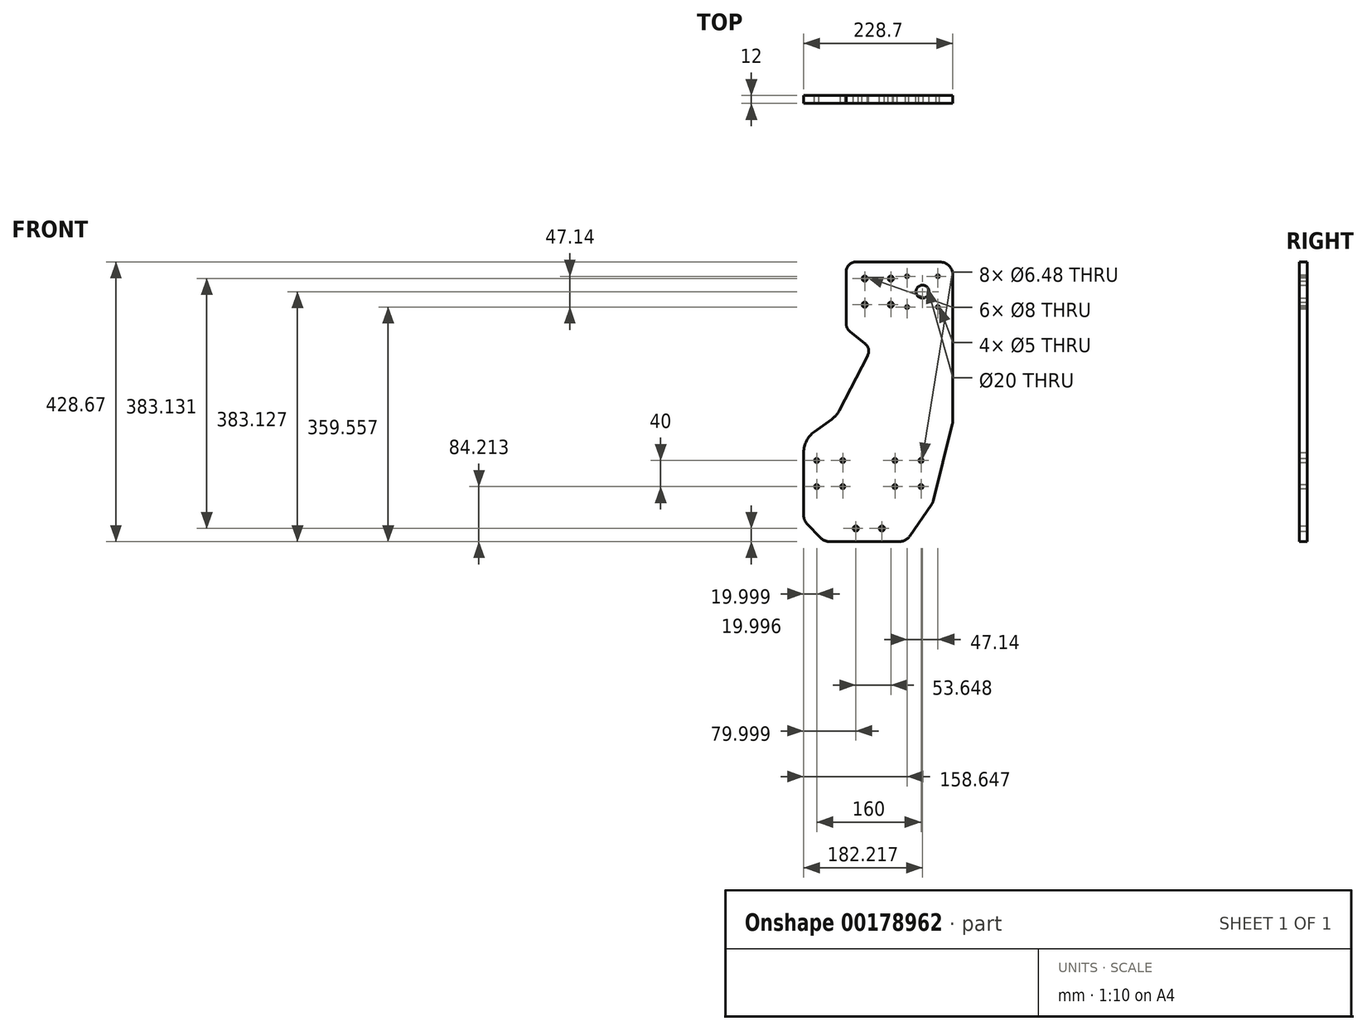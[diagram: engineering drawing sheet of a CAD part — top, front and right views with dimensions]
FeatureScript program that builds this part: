
annotation { "Feature Type Name" : "Feature", "Feature Type Description" : "" }
export const myFeature = defineFeature(function(context is Context, id is Id, definition is map)
    precondition{}
    {
        {
            var Q0;
            Q0=qCreatedBy(makeId("Front.planeOp"),FACE);
            var sketch = newSketch(context, id + "F0", { "sketchPlane" : qUnion([Q0])});
            skLineSegment(sketch, "E0.top", {"start": v(85.23, 205) * mm, "end": v(25.3, 205) * mm});
            skPoint(sketch, "E0.middle", {"position": v(0, 0) * mm});
            skLineSegment(sketch, "E1", {"start": v(135.36, -38.58) * mm, "end": v(135.36, 185) * mm});
            skLineSegment(sketch, "E2", {"start": v(115.36, 205) * mm, "end": v(85.23, 205) * mm});
            skLineSegment(sketch, "E3", {"start": v(-50.18, -36.07) * mm, "end": v(-76.73, -55.2) * mm});
            skCircle(sketch, "E4", {"center": v(-73.34, -139.46) * mm, "radius": 3.24 * mm});
            skCircle(sketch, "E5", {"center": v(-73.34, -99.46) * mm, "radius": 3.24 * mm});
            skCircle(sketch, "E6", {"center": v(-33.34, -99.46) * mm, "radius": 3.24 * mm});
            skCircle(sketch, "E7", {"center": v(-33.34, -139.46) * mm, "radius": 3.24 * mm});
            skCircle(sketch, "E8", {"center": v(46.66, -99.46) * mm, "radius": 3.24 * mm});
            skCircle(sketch, "E9", {"center": v(46.66, -139.46) * mm, "radius": 3.24 * mm});
            skCircle(sketch, "E10", {"center": v(86.66, -139.46) * mm, "radius": 3.24 * mm});
            skCircle(sketch, "E11", {"center": v(86.66, -99.46) * mm, "radius": 3.24 * mm});
            skCircle(sketch, "E12", {"center": v(-13.34, -203.67) * mm, "radius": 4 * mm});
            skCircle(sketch, "E13", {"center": v(26.66, -203.67) * mm, "radius": 4 * mm});
            skPoint(sketch, "E14.orphan", {"position": v(-84.77, 205) * mm});
            skPoint(sketch, "E15.visualSharp", {"position": v(-92.99, -66.91) * mm});
            skArc(sketch, "E15.filletArc", {"start": v(-76.73, -55.2) * mm, "mid": v(-88.79, -69.1) * mm, "end": v(-93.34, -86.95) * mm});
            skCircle(sketch, "E16", {"center": v(0.3, 179.46) * mm, "radius": 4 * mm});
            skCircle(sketch, "E17", {"center": v(40.3, 179.46) * mm, "radius": 4 * mm});
            skCircle(sketch, "E18", {"center": v(0.3, 139.46) * mm, "radius": 4 * mm});
            skCircle(sketch, "E19", {"center": v(40.3, 139.46) * mm, "radius": 4 * mm});
            skCircle(sketch, "E20", {"center": v(65.3, 183.03) * mm, "radius": 2.5 * mm});
            skCircle(sketch, "E21", {"center": v(112.45, 183.03) * mm, "radius": 2.5 * mm});
            skCircle(sketch, "E22", {"center": v(65.3, 135.89) * mm, "radius": 2.5 * mm});
            skCircle(sketch, "E23", {"center": v(112.45, 135.89) * mm, "radius": 2.5 * mm});
            skCircle(sketch, "E24", {"center": v(88.88, 159.46) * mm, "radius": 10 * mm});
            skPoint(sketch, "E25.visualSharp", {"position": v(135.36, 205) * mm});
            skArc(sketch, "E25.filletArc", {"start": v(135.36, 185) * mm, "mid": v(129.5, 199.14) * mm, "end": v(115.36, 205) * mm});
            skPoint(sketch, "E26.orphan", {"position": v(-34.7, 179.46) * mm});
            skPoint(sketch, "E27.visualSharp", {"position": v(-22, 205) * mm});
            skPoint(sketch, "E28.orphan", {"position": v(-34.7, 139.46) * mm});
            skPoint(sketch, "E29.orphan", {"position": v(135.36, 128.58) * mm});
            skLineSegment(sketch, "E30", {"start": v(25.3, 205) * mm, "end": v(25.3, 205) * mm});
            skLineSegment(sketch, "E31", {"start": v(25.3, 205) * mm, "end": v(10.35, 205) * mm});
            skPoint(sketch, "E32.visualSharp", {"position": v(0.04, 128.58) * mm});
            skPoint(sketch, "E33.orphan", {"position": v(47.2, 128.58) * mm});
            skLineSegment(sketch, "E34", {"start": v(42.47, 120.22) * mm, "end": v(42.47, 120.22) * mm});
            skLineSegment(sketch, "E35", {"start": v(0.04, 128.58) * mm, "end": v(-2.03, 128.58) * mm});
            skPoint(sketch, "E36.visualSharp", {"position": v(-11.41, 128.58) * mm});
            skLineSegment(sketch, "E37", {"start": v(-93.34, -86.95) * mm, "end": v(-93.34, -135.08) * mm});
            skPoint(sketch, "E38.visualSharp", {"position": v(-43.06, -30.95) * mm});
            skArc(sketch, "E38.filletArc", {"start": v(-50.18, -36.07) * mm, "mid": v(-43.91, -30.47) * mm, "end": v(-38.96, -23.69) * mm});
            skPoint(sketch, "E39.end.orphan", {"position": v(-14.64, 179.46) * mm});
            skLineSegment(sketch, "E40", {"start": v(3.97, 59.83) * mm, "end": v(-38.6, -23.02) * mm});
            skPoint(sketch, "E41.visualSharp", {"position": v(-35.75, 205) * mm});
            skPoint(sketch, "E42.visualSharp", {"position": v(-35.75, 100.23) * mm});
            skPoint(sketch, "E43.visualSharp", {"position": v(10.35, 72.27) * mm});
            skPoint(sketch, "E44.visualSharp", {"position": v(-38.75, -23.32) * mm});
            skArc(sketch, "E44.filletArc", {"start": v(-38.96, -23.69) * mm, "mid": v(-38.77, -23.36) * mm, "end": v(-38.6, -23.02) * mm});
            skLineSegment(sketch, "E45", {"start": v(10.35, 205) * mm, "end": v(-13, 205) * mm});
            skLineSegment(sketch, "E46", {"start": v(-28, 190) * mm, "end": v(-28, 109.95) * mm});
            skLineSegment(sketch, "E47", {"start": v(-22.33, 98.2) * mm, "end": v(0.71, 79.92) * mm});
            skLineSegment(sketch, "E48", {"start": v(4.73, 61.31) * mm, "end": v(3.97, 59.83) * mm});
            skPoint(sketch, "E49.visualSharp", {"position": v(-28, 205) * mm});
            skArc(sketch, "E49.filletArc", {"start": v(-13, 205) * mm, "mid": v(-23.61, 200.6) * mm, "end": v(-28, 190) * mm});
            skPoint(sketch, "E50.visualSharp", {"position": v(-28, 102.7) * mm});
            skArc(sketch, "E50.filletArc", {"start": v(-28, 109.95) * mm, "mid": v(-26.51, 103.43) * mm, "end": v(-22.33, 98.2) * mm});
            skArc(sketch, "E51.filletArc", {"start": v(4.73, 61.31) * mm, "mid": v(6.05, 71.33) * mm, "end": v(0.71, 79.92) * mm});
            skLineSegment(sketch, "E52", {"start": v(-93.34, -135.08) * mm, "end": v(-93.34, -183.04) * mm});
            skLineSegment(sketch, "E53", {"start": v(-53.7, -223.67) * mm, "end": v(53.23, -223.67) * mm});
            skLineSegment(sketch, "E54", {"start": v(105.34, -161.24) * mm, "end": v(134.76, -43.42) * mm});
            skLineSegment(sketch, "E55", {"start": v(-87.83, -196.83) * mm, "end": v(-68.18, -217.46) * mm});
            skPoint(sketch, "E56.orphan", {"position": v(-93.34, -223.67) * mm});
            skPoint(sketch, "E57.visualSharp", {"position": v(-93.34, -191.04) * mm});
            skArc(sketch, "E57.filletArc", {"start": v(-93.34, -183.04) * mm, "mid": v(-91.91, -190.47) * mm, "end": v(-87.83, -196.83) * mm});
            skPoint(sketch, "E58.visualSharp", {"position": v(-62.27, -223.67) * mm});
            skArc(sketch, "E58.filletArc", {"start": v(-68.18, -217.46) * mm, "mid": v(-61.58, -222.06) * mm, "end": v(-53.7, -223.67) * mm});
            skLineSegment(sketch, "E59", {"start": v(69.67, -215.05) * mm, "end": v(102.39, -167.77) * mm});
            skPoint(sketch, "E60.orphan", {"position": v(89.75, -223.67) * mm});
            skPoint(sketch, "E61.visualSharp", {"position": v(63.7, -223.67) * mm});
            skArc(sketch, "E61.filletArc", {"start": v(53.23, -223.67) * mm, "mid": v(62.51, -221.39) * mm, "end": v(69.67, -215.05) * mm});
            skPoint(sketch, "E62.visualSharp", {"position": v(104.46, -164.78) * mm});
            skArc(sketch, "E62.filletArc", {"start": v(102.39, -167.77) * mm, "mid": v(104.16, -164.64) * mm, "end": v(105.34, -161.24) * mm});
            skPoint(sketch, "E63.visualSharp", {"position": v(135.36, -41.04) * mm});
            skArc(sketch, "E63.filletArc", {"start": v(134.76, -43.42) * mm, "mid": v(135.21, -41.02) * mm, "end": v(135.36, -38.58) * mm});
            skSolve(sketch);
        }
        {
            var Q0;
            Q0=makeQuery(id+"F0.imprint","IMPRINT",FACE,{"disambiguationData":[TD([[makeQuery(id+"F0.imprint","IMPRINT",EDGE,{"derivedFrom":sQuery(id+"F0.wireOp",EDGE,"E0.top")}),1.0]])]});
            extrude(context, id + "F1", {"entities" : qUnion([Q0]), "depth" : 12 * mm});
        }
    });
